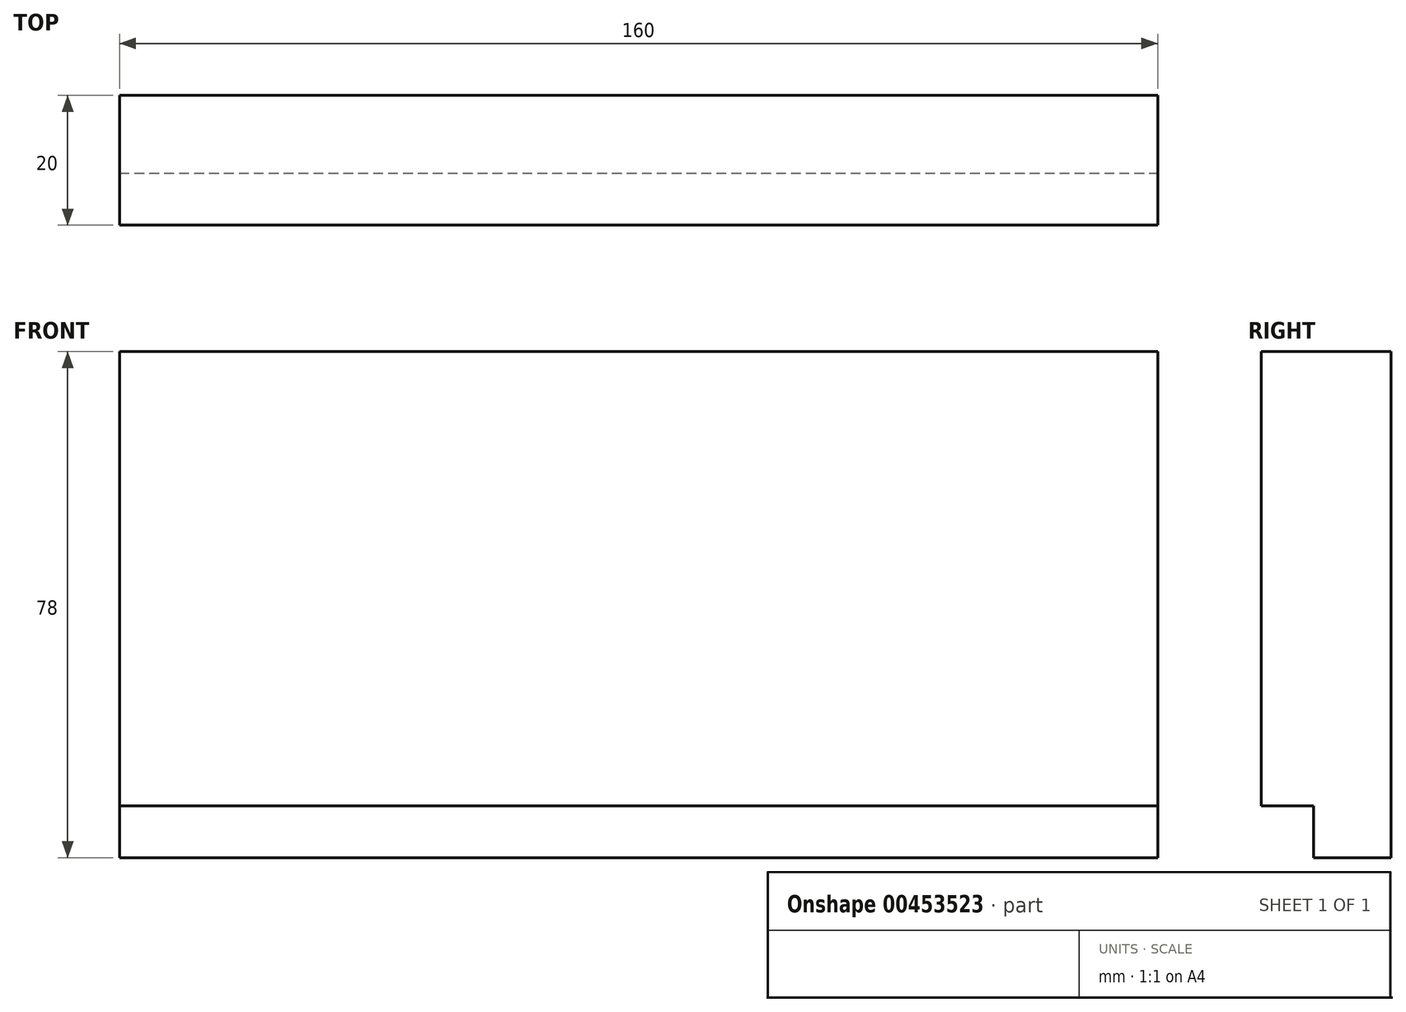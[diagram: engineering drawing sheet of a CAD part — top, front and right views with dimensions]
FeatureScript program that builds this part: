
annotation { "Feature Type Name" : "Feature", "Feature Type Description" : "" }
export const myFeature = defineFeature(function(context is Context, id is Id, definition is map)
    precondition{}
    {
        {
            var Q0;
            Q0=qCreatedBy(makeId("Front.planeOp"),FACE);
            var sketch = newSketch(context, id + "F0", { "sketchPlane" : qUnion([Q0])});
            skLineSegment(sketch, "E0.bottom", {"start": v(80, -39) * mm, "end": v(-80, -39) * mm});
            skLineSegment(sketch, "E0.top", {"start": v(80, 39) * mm, "end": v(-80, 39) * mm});
            skLineSegment(sketch, "E0.left", {"start": v(80, -39) * mm, "end": v(80, 39) * mm});
            skLineSegment(sketch, "E0.right", {"start": v(-80, -39) * mm, "end": v(-80, 39) * mm});
            skPoint(sketch, "E0.middle", {"position": v(0, 0) * mm});
            skLineSegment(sketch, "E1", {"start": v(-80, -31) * mm, "end": v(80, -31) * mm});
            skSolve(sketch);
        }
        {
            var Q0;
            {var subQ0=sQuery(id+"F0.wireOp",EDGE,"E0.top");Q0=makeQuery(id+"F0.imprint","IMPRINT",FACE,{"disambiguationData":[TD([[makeQuery(id+"F0.imprint","IMPRINT",EDGE,{"derivedFrom":subQ0}),1.0]])]});}
            extrude(context, id + "F1", {"entities" : qUnion([Q0]), "depth" : 20 * mm});
        }
        {
            var Q0;
            {var subQ0=sQuery(id+"F0.wireOp",EDGE,"E0.top");Q0=makeQuery(id+"F0.imprint","IMPRINT",FACE,{"disambiguationData":[TD([[makeQuery(id+"F0.imprint","IMPRINT",EDGE,{"derivedFrom":subQ0}),1.0]])]});}
            var Q1;
            {var subQ0=sQuery(id+"F0.wireOp",EDGE,"E0.bottom");Q1=makeQuery(id+"F0.imprint","IMPRINT",FACE,{"disambiguationData":[TD([[makeQuery(id+"F0.imprint","IMPRINT",EDGE,{"derivedFrom":subQ0}),-1.0]])]});}
            extrude(context, id + "F2", {"entities" : qUnion([Q0, Q1]), "operationType" : NewBodyOperationType.ADD, "depth" : 12 * mm});
        }
    });
